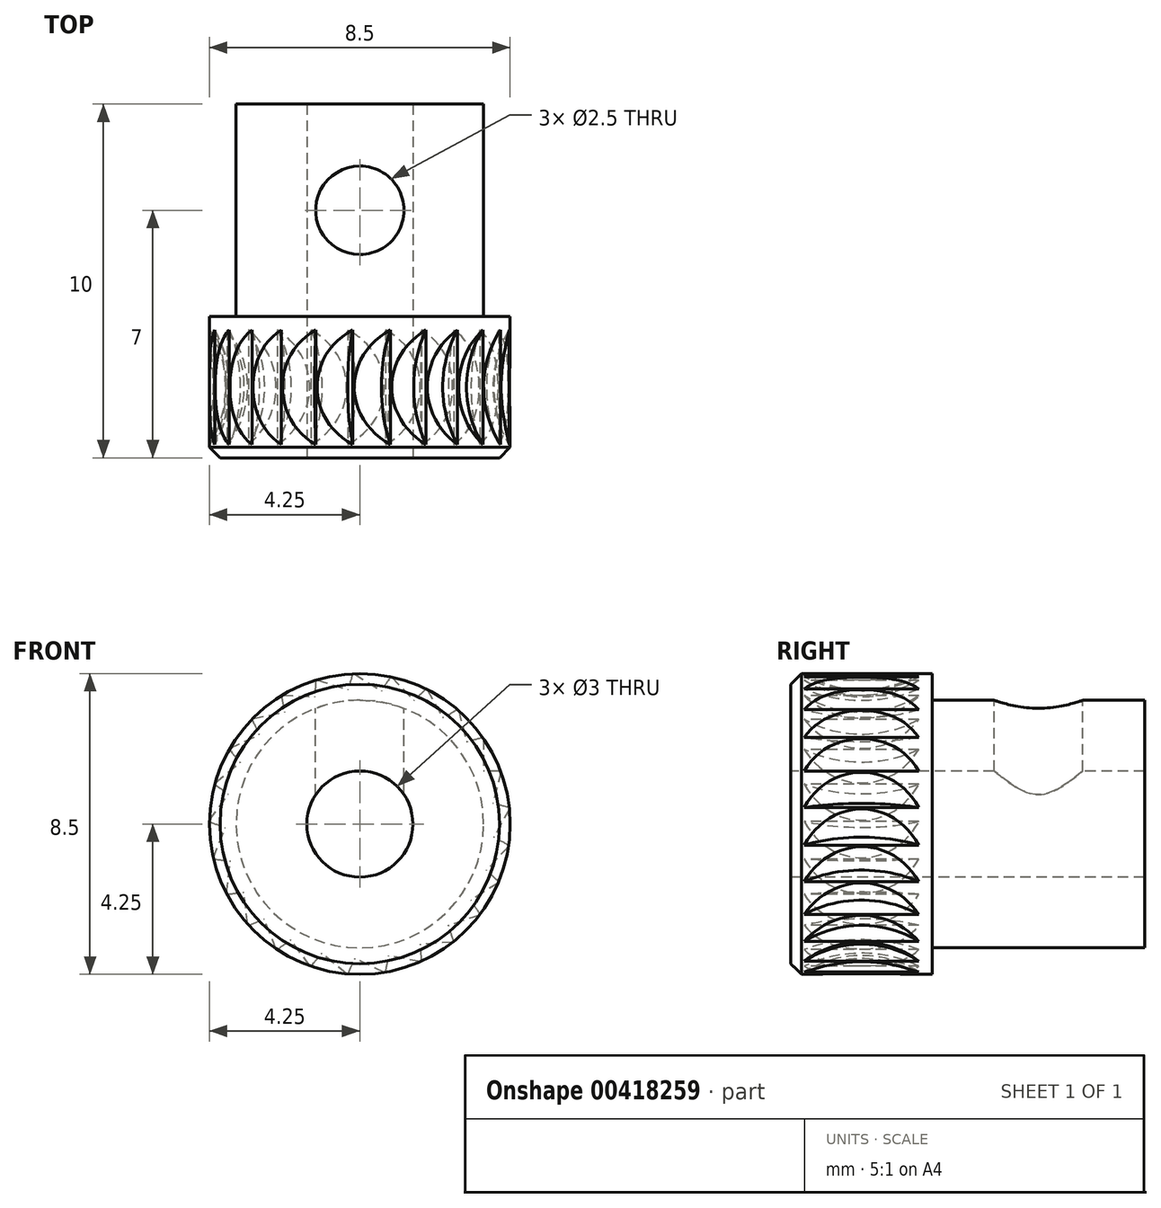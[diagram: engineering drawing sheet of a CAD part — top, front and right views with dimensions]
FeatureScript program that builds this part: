
annotation { "Feature Type Name" : "Feature", "Feature Type Description" : "" }
export const myFeature = defineFeature(function(context is Context, id is Id, definition is map)
    precondition{}
    {
        {
            var Q0;
            Q0=qCreatedBy(makeId("Front.planeOp"),FACE);
            var sketch = newSketch(context, id + "F0", { "sketchPlane" : qUnion([Q0])});
            skCircle(sketch, "E0", {"center": v(0, -1.5) * mm, "radius": 4.25 * mm});
            skSolve(sketch);
        }
        {
            var Q0;
            Q0=makeQuery(id+"F0.imprint","IMPRINT",FACE,{"disambiguationData":[TD([[makeQuery(id+"F0.imprint","IMPRINT",EDGE,{"derivedFrom":sQuery(id+"F0.wireOp",EDGE,"E0")}),1.0]])]});
            extrude(context, id + "F1", {"entities" : qUnion([Q0]), "oppositeDirection" : true, "depth" : 10 * mm});
        }
        {
            var Q0;
            Q0=qCreatedBy(makeId("Top.planeOp"),FACE);
            var sketch = newSketch(context, id + "F2", { "sketchPlane" : qUnion([Q0])});
            skCircle(sketch, "E1", {"center": v(6.5, 2) * mm, "radius": 3 * mm});
            skSolve(sketch);
        }
        {
            var Q0;
            Q0=qSketchRegion(id+"F2",true);
            extrude(context, id + "F3", {"entities" : qUnion([Q0]), "depth" : 10 * mm});
        }
        {
            var Q0;
            Q0=makeQuery(id+"F3.opExtrude","SWEPT_BODY",BODY,{"disambiguationData":[OSD([sQuery(id+"F2.wireOp",EDGE,"E1")])]});
            var Q1;
            Q1=makeQuery(id+"F1.opExtrude","CAP_EDGE",EDGE,{"disambiguationData":[OSD([sQuery(id+"F0.wireOp",EDGE,"E0")])],"isStart":true});
            circularPattern(context, id + "F4", {"operationType" : NewBodyOperationType.REMOVE, "entities" : qUnion([Q0]), "axis" : qUnion([Q1]), "angle" : 360 * degree, "instanceCount" : 25, "equalSpace" : true});
        }
        {
            var Q0;
            Q0=sQuery(id+"F0.wireOp",VERTEX,"E0.center");
            var Q1;
            Q1=makeQuery(id+"F1.opExtrude","SWEPT_BODY",BODY,{"disambiguationData":[OSD([sQuery(id+"F0.wireOp",EDGE,"E0")])]});
            hole(context, id + "F5", {"style" : HoleStyle.SIMPLE, "endStyle" : HoleEndStyle.THROUGH, "holeDiameter" : 3 * mm, "isTappedThrough" : true, "tappedDepth" : 12 * mm, "tapClearance" : 3, "locations" : qUnion([Q0]), "scope" : qUnion([Q1])});
        }
        {
            var Q0;
            Q0=makeQuery(id+"F1.opExtrude","CAP_FACE",FACE,{"disambiguationData":[OSD([sQuery(id+"F0.wireOp",EDGE,"E0")])],"isStart":false});
            var sketch = newSketch(context, id + "F6", { "sketchPlane" : qUnion([Q0])});
            skCircle(sketch, "E2", {"center": v(0, -1.5) * mm, "radius": 3.5 * mm});
            skSolve(sketch);
        }
        {
            var Q0;
            Q0=makeQuery(id+"F6.imprint","IMPRINT",FACE,{"disambiguationData":[TD([[makeQuery(id+"F6.imprint","IMPRINT",EDGE,{"derivedFrom":sQuery(id+"F6.wireOp",EDGE,"E2")}),-1.0]])]});
            extrude(context, id + "F7", {"entities" : qUnion([Q0]), "operationType" : NewBodyOperationType.REMOVE, "oppositeDirection" : true, "depth" : 6 * mm});
        }
        {
            var Q0;
            Q0=makeQuery(id+"F1.opExtrude","CAP_EDGE",EDGE,{"disambiguationData":[OSD([sQuery(id+"F0.wireOp",EDGE,"E0")])],"isStart":true});
            var Q1;
            Q1=makeQuery(id+"F5.hole-0.boolean.opBoolean","COPY",EDGE,{"derivedFrom":makeQuery(id+"F5.hole-0.opRevolve","SWEPT_EDGE",EDGE,{"disambiguationData":[OSD([sQuery(id+"F5.hole-0.sketch.wireOp",EDGE,"core_line_2"),sQuery(id+"F5.hole-0.sketch.wireOp",EDGE,"core_line_3")])]})});
            var Q2;
            Q2=makeQuery(id+"F5.hole-0.boolean.opBoolean","INTERSECT",EDGE,{"derivedFrom":[makeQuery(id+"F1.opExtrude","CAP_FACE",FACE,{"disambiguationData":[OSD([sQuery(id+"F0.wireOp",EDGE,"E0")])],"isStart":false}),makeQuery(id+"F5.hole-0.opRevolve","SWEPT_FACE",FACE,{"disambiguationData":[OSD([sQuery(id+"F5.hole-0.sketch.wireOp",EDGE,"core_line_2")])]})]});
            var Q3;
            Q3=makeQuery(id+"F1.opExtrude","CAP_EDGE",EDGE,{"disambiguationData":[OSD([sQuery(id+"F0.wireOp",EDGE,"E0")])],"isStart":false});
            var Q4;
            Q4=makeQuery(id+"F7.boolean.opBoolean","COPY",EDGE,{"derivedFrom":makeQuery(id+"F7.opExtrude","CAP_EDGE",EDGE,{"disambiguationData":[OSD([sQuery(id+"F0.wireOp",EDGE,"E0")])],"isStart":false})});
            var Q5;
            Q5=makeQuery(id+"F7.boolean.opBoolean","COPY",EDGE,{"derivedFrom":makeQuery(id+"F7.opExtrude","CAP_EDGE",EDGE,{"disambiguationData":[OSD([sQuery(id+"F6.wireOp",EDGE,"E2")])],"isStart":true})});
            chamfer(context, id + "F8", {"entities" : qUnion([Q0, Q1, Q2, Q3, Q4, Q5]), "width" : 0.3 * mm, "tangentPropagation" : true});
        }
        {
            var Q0;
            Q0=qCreatedBy(makeId("Top.planeOp"),FACE);
            cPlane(context, id + "F9", {"entities" : qUnion([Q0]), "cplaneType" : CPlaneType.OFFSET, "offset" : 2.5 * mm, "width" : 150 * mm, "height" : 150 * mm});
        }
        {
            var Q0;
            Q0=qCreatedBy(id+"F9.planeOp",FACE);
            var sketch = newSketch(context, id + "F10", { "sketchPlane" : qUnion([Q0])});
            skPoint(sketch, "E3", {"position": v(0, 7) * mm});
            skSolve(sketch);
        }
        {
            var Q0;
            Q0=sQuery(id+"F10.wireOp",VERTEX,"E3");
            var Q1;
            Q1=makeQuery(id+"F1.opExtrude","SWEPT_BODY",BODY,{"disambiguationData":[OSD([sQuery(id+"F0.wireOp",EDGE,"E0")])]});
            hole(context, id + "F11", {"style" : HoleStyle.C_SINK, "endStyle" : HoleEndStyle.BLIND, "holeDiameter" : 2.5 * mm, "cSinkDiameter" : 3.2 * mm, "cSinkAngle" : 90 * degree, "holeDepth" : 4 * mm, "isTappedThrough" : true, "tappedDepth" : 12 * mm, "tapClearance" : 3, "startFromSketch" : true, "locations" : qUnion([Q0]), "scope" : qUnion([Q1])});
        }
    });
